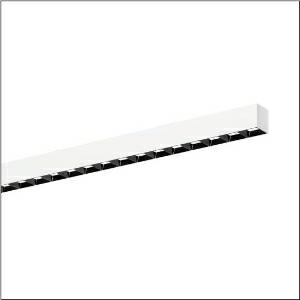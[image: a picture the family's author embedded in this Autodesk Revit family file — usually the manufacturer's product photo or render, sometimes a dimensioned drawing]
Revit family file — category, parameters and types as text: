
# Revit family: silica_21_51mx21dc4awb
name_source: partatom
category: Lighting Fixtures
units: mm (PartAtom-declared; Revit-internal decimal feet)

## family parameters
Cut with Voids When Loaded = No
Host = Face
Light Source = No
Part Type = Normal
Room Calculation Point = No
Round Connector Dimension = Use Diameter
Shared = No

## types (1)
- --- (1 x LED, 10800 lm, 64.8 W, 4000K)
    Apparent Load = 65 VA
    CIE Flux Codes = 87 99 100 100 100
    Color Rendering = 80
    Color Temperature = 4000K
    Default Elevation = 1800 mm
    Description = Silica 21, office luminaire, primary light control with darklight reflector, of PMMA, black, CAT 2 (L<= 3000cd/m²), light emission: direct distribution, primary light characteristic: symmetric, installation type: surface-mounted, LED, rated luminous flux: 10.800lm, luminous efficacy: 167lm/W, light colour: 840, colour temperature: 4000K, control gear: DALI 2, with terminal, 3+2-pole, max. 2.5mm², mains connection: 220..240V, AC, 50/60Hz, rated input power: 64.8W, luminaire housing, of aluminium, traffic white (RAL 9016), length: 3.004mm, width: 53mm, height: 53mm, protection rating (complete): IP20, insulation class (complete): insulation class I (protective earthing), certification: CE, permissible operating ambient temperature: 0..+35°C, standard: EN 50419, packaging unit: 1 piece
    Height = 53 mm
    Lamp = 1 x LED
    Lamp Light Flux = 10800 lm
    Lamp Power = 64.8 W
    Lamp count = 1
    Length = 3004 mm
    Luminous efficacy = 167 lm/W
    Manufacturer = Siteco
    ModVariant = No
    Model = 51MX21DC4AWB
    Mounting Place = Ceiling
    Mounting Type = Surface mounted
    Number of Poles = 1
    OnlyDefault = Yes
    Power Factor = 1
    Product Name = Silica 21
    Product group = office luminaire | ceiling mounted
    ProductGroupID = 301
    Protection Class = Protection class I
    Protection Degree = IP 20
    RLX_Detail_Level = 1
    RLX_Emergency_Light_Flux = 0 lm
    RLX_Emergency_Type = 0
    RLX_Emergency_Type_DB = No
    RlxData = <blob elided: 61849 chars, md5=e4ca79be>
    Socket = socket
    Standby Power = 0 W
    System Light Flux = 10800 lm
    System Power = 65 W
    Type Comments = factory setting: luminous flux: 100 % | dim-lin: 254 | 367 mA
    Type Image = l_1335873.jpg
    URL = http://relux.com
    VarID = @adj_124041
    Voltage = 0 V
    Weight = 0.00 kg
    Width = 53 mm

## geometry (parser evidence)
native form markers: Blend x4, Sweep x12
no freeform markers — native parametric forms only
